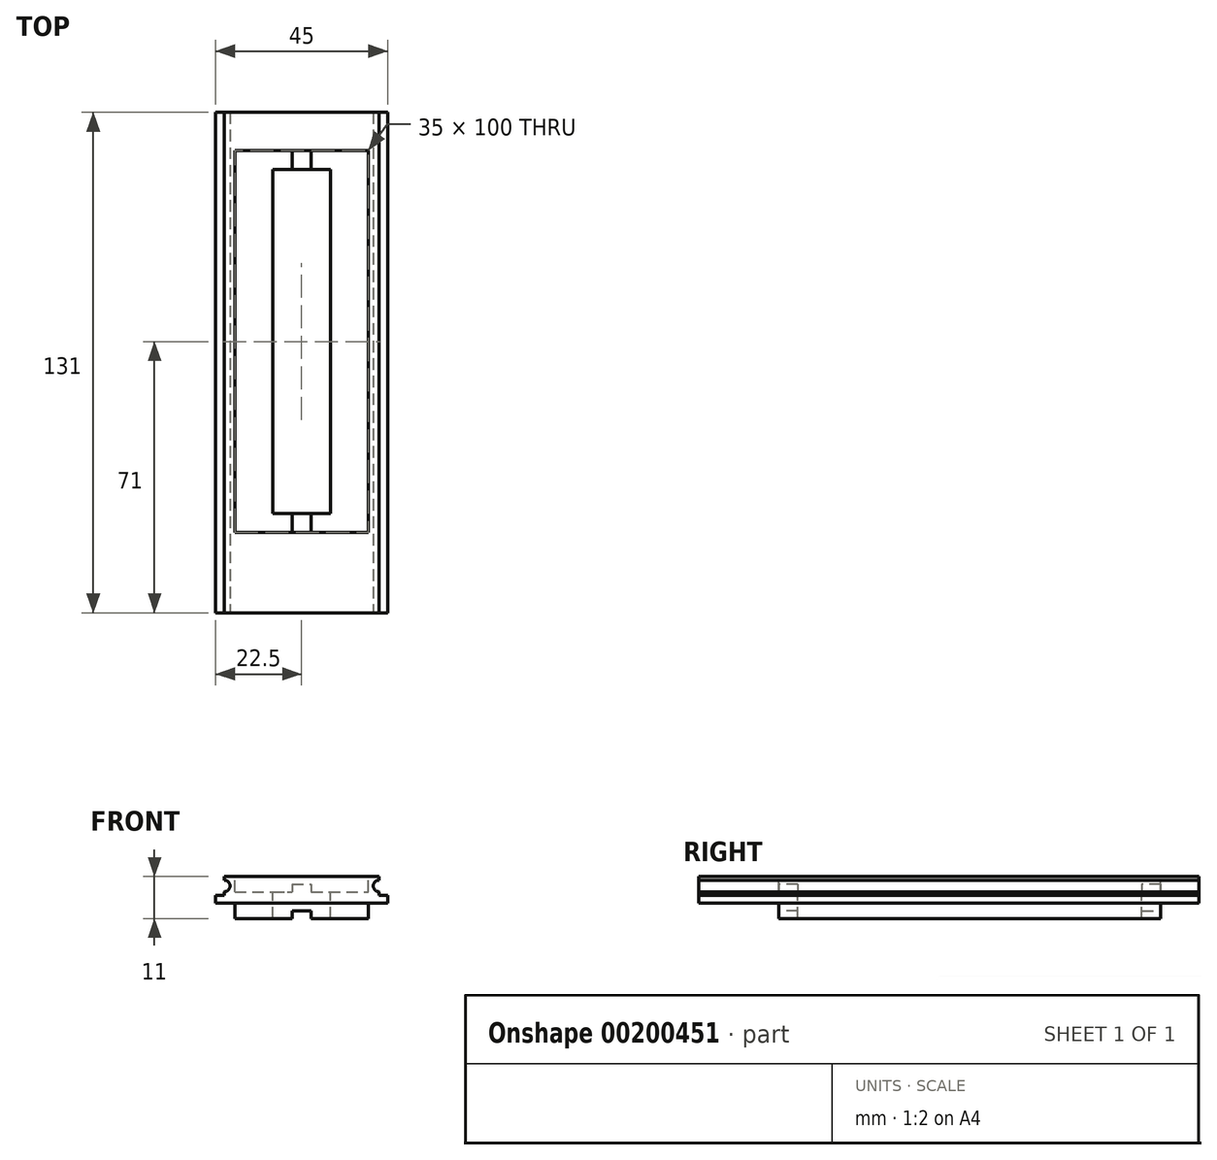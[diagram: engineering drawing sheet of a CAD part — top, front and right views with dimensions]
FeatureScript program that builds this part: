
annotation { "Feature Type Name" : "Feature", "Feature Type Description" : "" }
export const myFeature = defineFeature(function(context is Context, id is Id, definition is map)
    precondition{}
    {
        {
            var Q0;
            Q0=qCreatedBy(makeId("Top.planeOp"),FACE);
            var sketch = newSketch(context, id + "F0", { "sketchPlane" : qUnion([Q0])});
            skLineSegment(sketch, "E0.bottom", {"start": v(0, 0) * mm, "end": v(45, 0) * mm});
            skLineSegment(sketch, "E0.top", {"start": v(0, 131) * mm, "end": v(45, 131) * mm});
            skLineSegment(sketch, "E0.left", {"start": v(0, 0) * mm, "end": v(0, 131) * mm});
            skLineSegment(sketch, "E0.right", {"start": v(45, 0) * mm, "end": v(45, 131) * mm});
            skSolve(sketch);
        }
        {
            var Q0;
            Q0=qSketchRegion(id+"F0",true);
            extrude(context, id + "F1", {"entities" : qUnion([Q0]), "depth" : 2 * mm});
        }
        {
            var Q0;
            Q0=makeQuery(id+"F1.opExtrude","CAP_FACE",FACE,{"disambiguationData":[OSD([sQuery(id+"F0.wireOp",EDGE,"E0.bottom"),sQuery(id+"F0.wireOp",EDGE,"E0.top"),sQuery(id+"F0.wireOp",EDGE,"E0.left"),sQuery(id+"F0.wireOp",EDGE,"E0.right")])],"isStart":false});
            var sketch = newSketch(context, id + "F2", { "sketchPlane" : qUnion([Q0])});
            skLineSegment(sketch, "E1.bottom", {"start": v(2.25, 0) * mm, "end": v(42.75, 0) * mm});
            skLineSegment(sketch, "E1.top", {"start": v(2.25, 131) * mm, "end": v(42.75, 131) * mm});
            skLineSegment(sketch, "E1.left", {"start": v(2.25, 0) * mm, "end": v(2.25, 131) * mm});
            skLineSegment(sketch, "E1.right", {"start": v(42.75, 0) * mm, "end": v(42.75, 131) * mm});
            skSolve(sketch);
        }
        {
            var Q0;
            Q0=qSketchRegion(id+"F2",true);
            extrude(context, id + "F3", {"entities" : qUnion([Q0]), "operationType" : NewBodyOperationType.ADD, "depth" : 5 * mm});
        }
        {
            var Q0;
            Q0=makeQuery(id+"F3.opExtrude","CAP_FACE",FACE,{"disambiguationData":[OSD([sQuery(id+"F2.wireOp",EDGE,"E1.bottom"),sQuery(id+"F2.wireOp",EDGE,"E1.top"),sQuery(id+"F2.wireOp",EDGE,"E1.left"),sQuery(id+"F2.wireOp",EDGE,"E1.right")])],"isStart":false});
            var sketch = newSketch(context, id + "F4", { "sketchPlane" : qUnion([Q0])});
            skLineSegment(sketch, "E2.bottom", {"start": v(15, 116) * mm, "end": v(30, 116) * mm});
            skLineSegment(sketch, "E2.top", {"start": v(15, 26) * mm, "end": v(30, 26) * mm});
            skLineSegment(sketch, "E2.left", {"start": v(15, 116) * mm, "end": v(15, 26) * mm});
            skLineSegment(sketch, "E2.right", {"start": v(30, 116) * mm, "end": v(30, 26) * mm});
            skSolve(sketch);
        }
        {
            var Q0;
            Q0=makeQuery(id+"F3.opExtrude","CAP_FACE",FACE,{"disambiguationData":[OSD([sQuery(id+"F2.wireOp",EDGE,"E1.bottom"),sQuery(id+"F2.wireOp",EDGE,"E1.top"),sQuery(id+"F2.wireOp",EDGE,"E1.left"),sQuery(id+"F2.wireOp",EDGE,"E1.right")])],"isStart":false});
            var sketch = newSketch(context, id + "F5", { "sketchPlane" : qUnion([Q0])});
            skLineSegment(sketch, "E3.bottom", {"start": v(5, 121) * mm, "end": v(40, 121) * mm});
            skLineSegment(sketch, "E3.top", {"start": v(5, 21) * mm, "end": v(40, 21) * mm});
            skLineSegment(sketch, "E3.left", {"start": v(5, 121) * mm, "end": v(5, 21) * mm});
            skLineSegment(sketch, "E3.right", {"start": v(40, 121) * mm, "end": v(40, 21) * mm});
            skSolve(sketch);
        }
        {
            var Q0;
            Q0=qSketchRegion(id+"F5",true);
            extrude(context, id + "F6", {"entities" : qUnion([Q0]), "operationType" : NewBodyOperationType.REMOVE, "oppositeDirection" : true, "depth" : 4 * mm});
        }
        {
            var Q0;
            Q0=makeQuery(id+"F6.boolean.opBoolean","COPY",FACE,{"derivedFrom":makeQuery(id+"F6.opExtrude","CAP_FACE",FACE,{"disambiguationData":[OSD([sQuery(id+"F5.wireOp",EDGE,"E3.bottom"),sQuery(id+"F5.wireOp",EDGE,"E3.top"),sQuery(id+"F5.wireOp",EDGE,"E3.left"),sQuery(id+"F5.wireOp",EDGE,"E3.right")])],"isStart":false})});
            var sketch = newSketch(context, id + "F7", { "sketchPlane" : qUnion([Q0])});
            skLineSegment(sketch, "E4.bottom", {"start": v(20, 121) * mm, "end": v(25, 121) * mm});
            skLineSegment(sketch, "E4.top", {"start": v(20, 21) * mm, "end": v(25, 21) * mm});
            skLineSegment(sketch, "E4.left", {"start": v(20, 121) * mm, "end": v(20, 21) * mm});
            skLineSegment(sketch, "E4.right", {"start": v(25, 121) * mm, "end": v(25, 21) * mm});
            skSolve(sketch);
        }
        {
            var Q0;
            Q0=qSketchRegion(id+"F7",true);
            extrude(context, id + "F8", {"entities" : qUnion([Q0]), "operationType" : NewBodyOperationType.ADD, "depth" : 2 * mm});
        }
        {
            var Q0;
            Q0=qSketchRegion(id+"F4",true);
            extrude(context, id + "F9", {"entities" : qUnion([Q0]), "operationType" : NewBodyOperationType.REMOVE, "endBound" : BoundingType.THROUGH_ALL, "oppositeDirection" : true, "depth" : 25.4 * mm});
        }
        {
            var Q0;
            Q0=makeQuery(id+"F1.opExtrude","CAP_FACE",FACE,{"disambiguationData":[OSD([sQuery(id+"F0.wireOp",EDGE,"E0.bottom"),sQuery(id+"F0.wireOp",EDGE,"E0.top"),sQuery(id+"F0.wireOp",EDGE,"E0.left"),sQuery(id+"F0.wireOp",EDGE,"E0.right")])],"isStart":true});
            var sketch = newSketch(context, id + "F10", { "sketchPlane" : qUnion([Q0])});
            skLineSegment(sketch, "E5.bottom", {"start": v(20, -116) * mm, "end": v(25, -116) * mm});
            skLineSegment(sketch, "E5.top", {"start": v(20, -121) * mm, "end": v(25, -121) * mm});
            skLineSegment(sketch, "E5.left", {"start": v(20, -116) * mm, "end": v(20, -121) * mm});
            skLineSegment(sketch, "E5.right", {"start": v(25, -116) * mm, "end": v(25, -121) * mm});
            skPoint(sketch, "E6.firstSnap0", {"position": v(22.5, -26) * mm});
            skLineSegment(sketch, "E6.bottom", {"start": v(25, -26) * mm, "end": v(20, -26) * mm});
            skLineSegment(sketch, "E6.top", {"start": v(25, -21) * mm, "end": v(20, -21) * mm});
            skLineSegment(sketch, "E6.left", {"start": v(25, -26) * mm, "end": v(25, -21) * mm});
            skLineSegment(sketch, "E6.right", {"start": v(20, -26) * mm, "end": v(20, -21) * mm});
            skSolve(sketch);
        }
        {
            var Q0;
            Q0=makeQuery(id+"F10.imprint","IMPRINT",FACE,{"disambiguationData":[TD([[makeQuery(id+"F10.imprint","IMPRINT",EDGE,{"derivedFrom":sQuery(id+"F10.wireOp",EDGE,"E5.top")}),-1.0]])]});
            var sketch = newSketch(context, id + "F11", { "sketchPlane" : qUnion([Q0])});
            skLineSegment(sketch, "E7.bottom", {"start": v(5, -21) * mm, "end": v(15, -21) * mm});
            skLineSegment(sketch, "E7.top", {"start": v(5, -121) * mm, "end": v(15, -121) * mm});
            skLineSegment(sketch, "E7.left", {"start": v(5, -21) * mm, "end": v(5, -121) * mm});
            skLineSegment(sketch, "E7.right", {"start": v(15, -21) * mm, "end": v(15, -121) * mm});
            skLineSegment(sketch, "E8.bottom", {"start": v(30, -21) * mm, "end": v(40, -21) * mm});
            skLineSegment(sketch, "E8.top", {"start": v(30, -121) * mm, "end": v(40, -121) * mm});
            skLineSegment(sketch, "E8.left", {"start": v(30, -21) * mm, "end": v(30, -121) * mm});
            skLineSegment(sketch, "E8.right", {"start": v(40, -21) * mm, "end": v(40, -121) * mm});
            skSolve(sketch);
        }
        {
            var Q0;
            Q0=makeQuery(id+"F10.imprint","IMPRINT",FACE,{"disambiguationData":[TD([[makeQuery(id+"F10.imprint","IMPRINT",EDGE,{"derivedFrom":sQuery(id+"F10.wireOp",EDGE,"E5.top")}),-1.0]])]});
            var sketch = newSketch(context, id + "F12", { "sketchPlane" : qUnion([Q0])});
            skLineSegment(sketch, "E9.bottom", {"start": v(15, -21) * mm, "end": v(20, -21) * mm});
            skLineSegment(sketch, "E9.top", {"start": v(15, -26) * mm, "end": v(20, -26) * mm});
            skLineSegment(sketch, "E9.left", {"start": v(15, -21) * mm, "end": v(15, -26) * mm});
            skLineSegment(sketch, "E9.right", {"start": v(20, -21) * mm, "end": v(20, -26) * mm});
            skLineSegment(sketch, "E10.bottom", {"start": v(25, -21) * mm, "end": v(30, -21) * mm});
            skLineSegment(sketch, "E10.top", {"start": v(25, -26) * mm, "end": v(30, -26) * mm});
            skLineSegment(sketch, "E10.left", {"start": v(25, -21) * mm, "end": v(25, -26) * mm});
            skLineSegment(sketch, "E10.right", {"start": v(30, -21) * mm, "end": v(30, -26) * mm});
            skLineSegment(sketch, "E11.bottom", {"start": v(25, -116) * mm, "end": v(30, -116) * mm});
            skLineSegment(sketch, "E11.top", {"start": v(25, -121) * mm, "end": v(30, -121) * mm});
            skLineSegment(sketch, "E11.left", {"start": v(25, -116) * mm, "end": v(25, -121) * mm});
            skLineSegment(sketch, "E11.right", {"start": v(30, -116) * mm, "end": v(30, -121) * mm});
            skLineSegment(sketch, "E12.bottom", {"start": v(15, -116) * mm, "end": v(20, -116) * mm});
            skLineSegment(sketch, "E12.top", {"start": v(15, -121) * mm, "end": v(20, -121) * mm});
            skLineSegment(sketch, "E12.left", {"start": v(15, -116) * mm, "end": v(15, -121) * mm});
            skLineSegment(sketch, "E12.right", {"start": v(20, -116) * mm, "end": v(20, -121) * mm});
            skSolve(sketch);
        }
        {
            var Q0;
            Q0=qSketchRegion(id+"F10",true);
            extrude(context, id + "F13", {"entities" : qUnion([Q0]), "operationType" : NewBodyOperationType.ADD, "depth" : 2 * mm});
        }
        {
            var Q0;
            Q0=qSketchRegion(id+"F12",true);
            extrude(context, id + "F14", {"entities" : qUnion([Q0]), "operationType" : NewBodyOperationType.ADD, "depth" : 4 * mm});
        }
        {
            var Q0;
            Q0=qSketchRegion(id+"F11",true);
            extrude(context, id + "F15", {"entities" : qUnion([Q0]), "operationType" : NewBodyOperationType.ADD, "depth" : 4 * mm});
        }
        {
            var Q0;
            Q0=makeQuery(id+"F3.boolean.opBoolean","MERGE",FACE,{"derivedFrom":[makeQuery(id+"F1.opExtrude","SWEPT_FACE",FACE,{"disambiguationData":[OSD([sQuery(id+"F0.wireOp",EDGE,"E0.bottom")])]}),makeQuery(id+"F3.opExtrude","SWEPT_FACE",FACE,{"disambiguationData":[OSD([sQuery(id+"F2.wireOp",EDGE,"E1.bottom")])]})]});
            var sketch = newSketch(context, id + "F16", { "sketchPlane" : qUnion([Q0])});
            skCircle(sketch, "E13", {"center": v(2.25, 4.5) * mm, "radius": 1.5 * mm});
            skCircle(sketch, "E14", {"center": v(42.75, 4.5) * mm, "radius": 1.5 * mm});
            skSolve(sketch);
        }
        {
            var Q0;
            Q0 = qSketchRegion(id + "F16", true);
            extrude(context, id + "F17", {"entities" : qUnion([Q0]), "operationType" : NewBodyOperationType.REMOVE, "endBound" : BoundingType.THROUGH_ALL, "oppositeDirection" : true, "depth" : 25.4 * mm});
        }
    });
